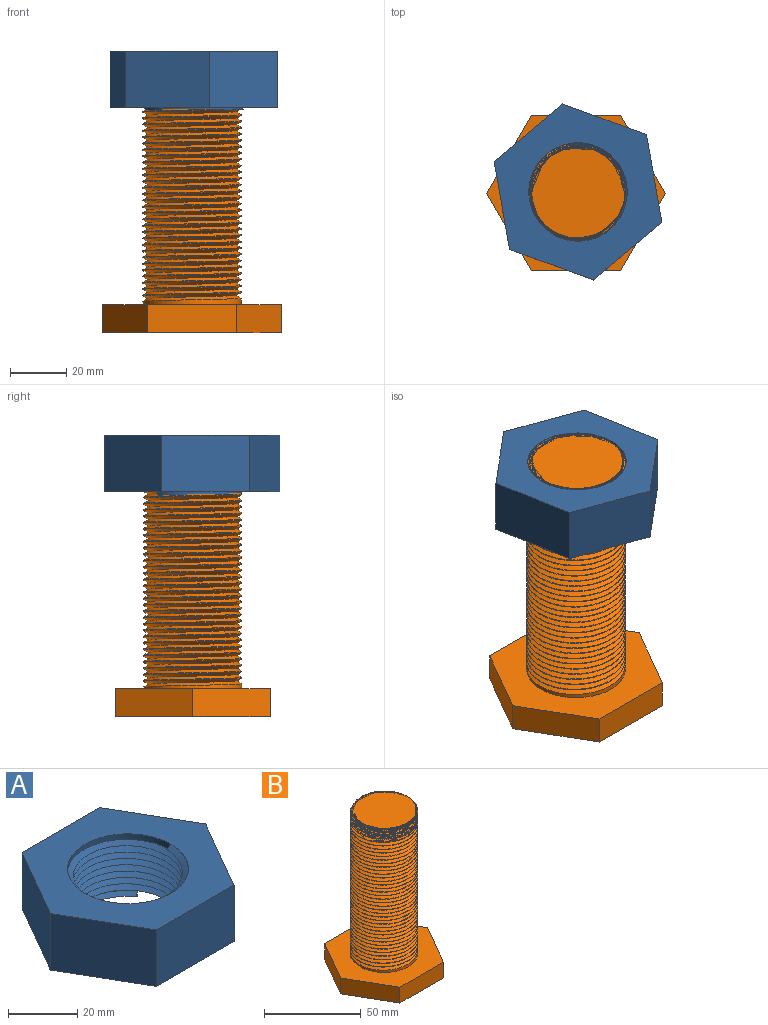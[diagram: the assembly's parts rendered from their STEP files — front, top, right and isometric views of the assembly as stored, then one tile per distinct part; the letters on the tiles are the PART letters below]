
ASSEMBLY  parts=2 mates=1
PART A: 14 faces, bbox 63.5x55x22.2 mm
  f0: cylinder r=17.5mm len=35mm, axis (0,0,-1), area 449.1mm2, adj f7,f8,f10,f12,f13
  f1: plane 27.5x20mm, normal (-0.87,-0.5,0), area 635.1mm2, adj f2,f6,f7,f8
  f2: plane 31.75x20mm, normal (0,-1,0), area 635.1mm2, adj f1,f3,f7,f8
  f3: plane 27.5x20mm, normal (0.87,-0.5,0), area 635.1mm2, adj f2,f4,f7,f8
  f4: plane 27.5x20mm, normal (0.87,0.5,0), area 635.1mm2, adj f3,f5,f7,f8
  f5: plane 31.75x20mm, normal (0,1,0), area 635.1mm2, adj f4,f6,f7,f8
  f6: plane 27.5x20mm, normal (-0.87,0.5,0), area 635.1mm2, adj f1,f5,f7,f8
  f7: plane 63.51x55mm, normal (0,0,1), area 1657.6mm2, adj f0,f1,f2,f3,f4,f5,f6
  f8: plane 63.51x55mm, normal (0,0,-1), area 1657.6mm2, adj f0,f1,f2,f3,f4,f5,f6,f9
  f9: cylinder r=17.5mm len=35mm, axis (0,0,-1), area 97.8mm2, adj f8,f11,f13
  f10: plane 2x1.73mm, normal (0,1,0), area 1.7mm2, adj f0,f12,f13
  f11: plane 2x1.4mm, normal (0.59,-0.81,0), area 1.7mm2, adj f9,f12,f13
  f12: bspline ~40.41x35mm, area 1860mm2, adj f0,f10,f11,f13
  f13: bspline ~40.41x35mm, area 1865.7mm2, adj f0,f9,f10,f11,f12
PART B: 13 faces, bbox 64.7x56.2x102.4 mm
  f0: cylinder r=17.5mm len=90mm, axis (0,0,-1), area 965.4mm2, adj f7,f9,f10,f11,f12
  f1: plane 27.5x15.88mm, normal (-0.87,-0.5,0), area 317.5mm2, adj f2,f6,f7,f8
  f2: plane 31.75x10mm, normal (0,-1,0), area 317.5mm2, adj f1,f3,f7,f8
  f3: plane 27.5x15.88mm, normal (0.87,-0.5,0), area 317.5mm2, adj f2,f4,f7,f8
  f4: plane 27.5x15.88mm, normal (0.87,0.5,0), area 317.5mm2, adj f3,f5,f7,f8
  f5: plane 31.75x10mm, normal (0,1,0), area 317.5mm2, adj f4,f6,f7,f8
  f6: plane 27.5x15.88mm, normal (-0.87,0.5,0), area 317.5mm2, adj f1,f5,f7,f8
  f7: plane 63.51x55mm, normal (0,0,1), area 1657.6mm2, adj f0,f1,f2,f3,f4,f5,f6
  f8: plane 63.51x55mm, normal (0,0,-1), area 2619.7mm2, adj f1,f2,f3,f4,f5,f6
  f9: plane 34.7x34.69mm, normal (0,0,1), area 880.3mm2, adj f0,f11,f12
  f10: plane 2x1.73mm, normal (0,1,0), area 1.7mm2, adj f0,f11,f12
  f11: bspline ~91x40.41mm, area 8299.7mm2, adj f0,f9,f10,f12
  f12: bspline ~90.25x40.41mm, area 8249.9mm2, adj f0,f9,f10,f11
PLACE A rot(axis=(0,0,1),100deg) t=(-50.59,-19.8,108.32)mm
PLACE B t=(-51.31,-20.06,28.32)mm
MATE revolute A.f0 <-> B.f9  axis (0,0,1) through (-50.59,-19.8,128.32)mm
